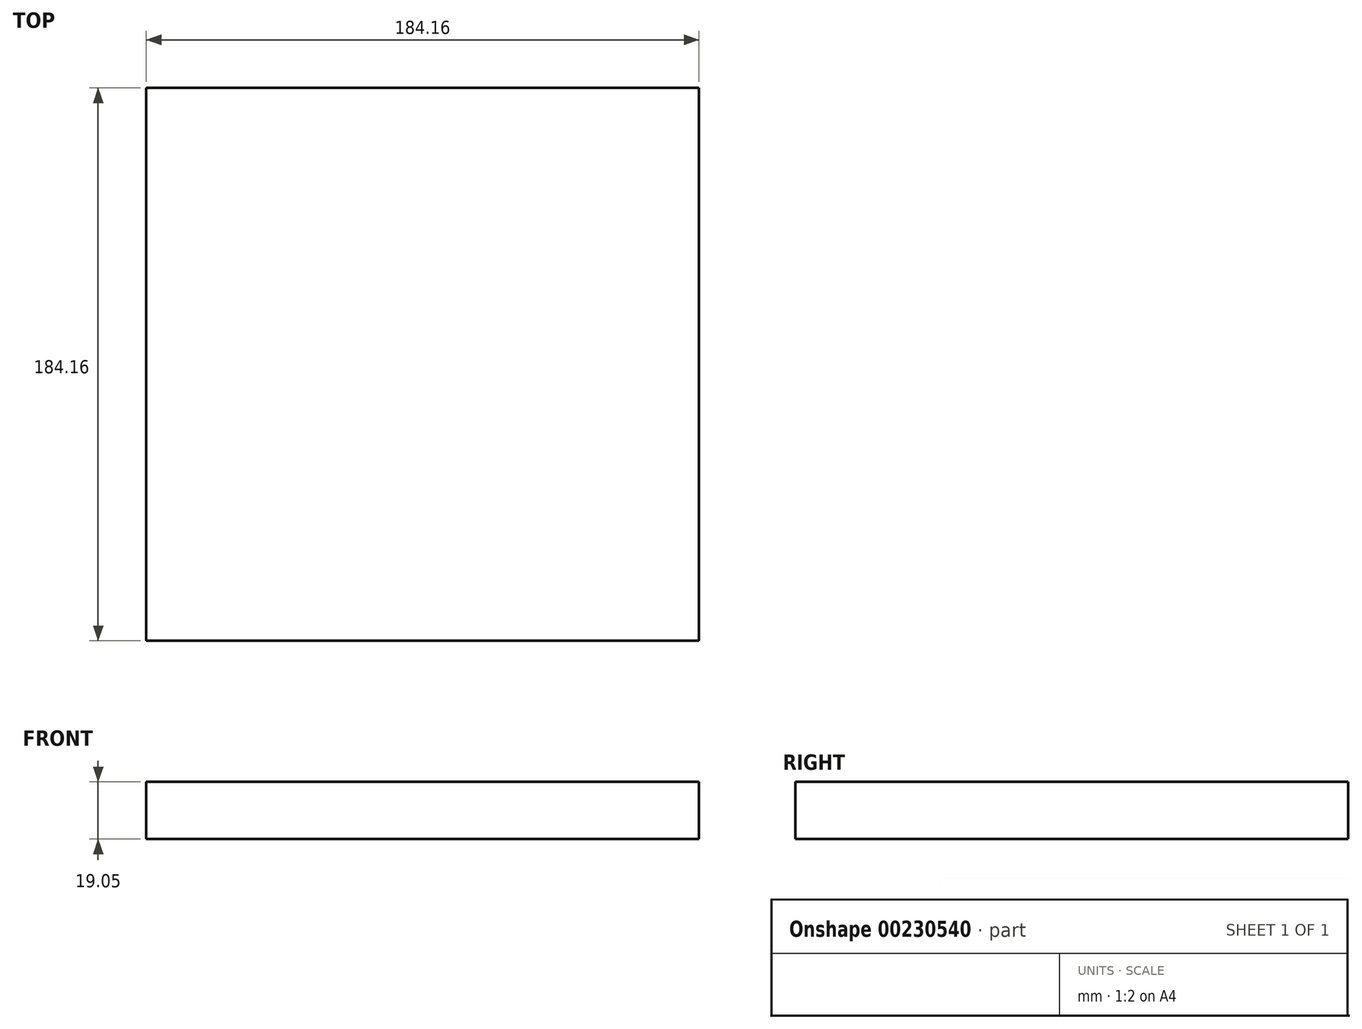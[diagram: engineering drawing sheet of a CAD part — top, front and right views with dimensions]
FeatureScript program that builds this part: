
annotation { "Feature Type Name" : "Feature", "Feature Type Description" : "" }
export const myFeature = defineFeature(function(context is Context, id is Id, definition is map)
    precondition{}
    {
        {
            var Q0;
            Q0=qCreatedBy(makeId("Top.planeOp"),FACE);
            var sketch = newSketch(context, id + "F0", { "sketchPlane" : qUnion([Q0])});
            skLineSegment(sketch, "E0.bottom", {"start": v(92.08, -92.07) * mm, "end": v(-92.07, -92.07) * mm});
            skLineSegment(sketch, "E0.top", {"start": v(92.07, 92.08) * mm, "end": v(-92.08, 92.08) * mm});
            skLineSegment(sketch, "E0.left", {"start": v(92.08, -92.07) * mm, "end": v(92.07, 92.08) * mm});
            skLineSegment(sketch, "E0.right", {"start": v(-92.08, -92.07) * mm, "end": v(-92.08, 92.08) * mm});
            skPoint(sketch, "E0.middle", {"position": v(0, 0) * mm});
            skSolve(sketch);
        }
        {
            var Q0;
            Q0=makeQuery(id+"F0.imprint","IMPRINT",FACE,{"disambiguationData":[TD([[makeQuery(id+"F0.imprint","IMPRINT",EDGE,{"derivedFrom":sQuery(id+"F0.wireOp",EDGE,"E0.bottom")}),-1.0]])]});
            extrude(context, id + "F1", {"entities" : qUnion([Q0]), "depth" : 19.05 * mm});
        }
    });
